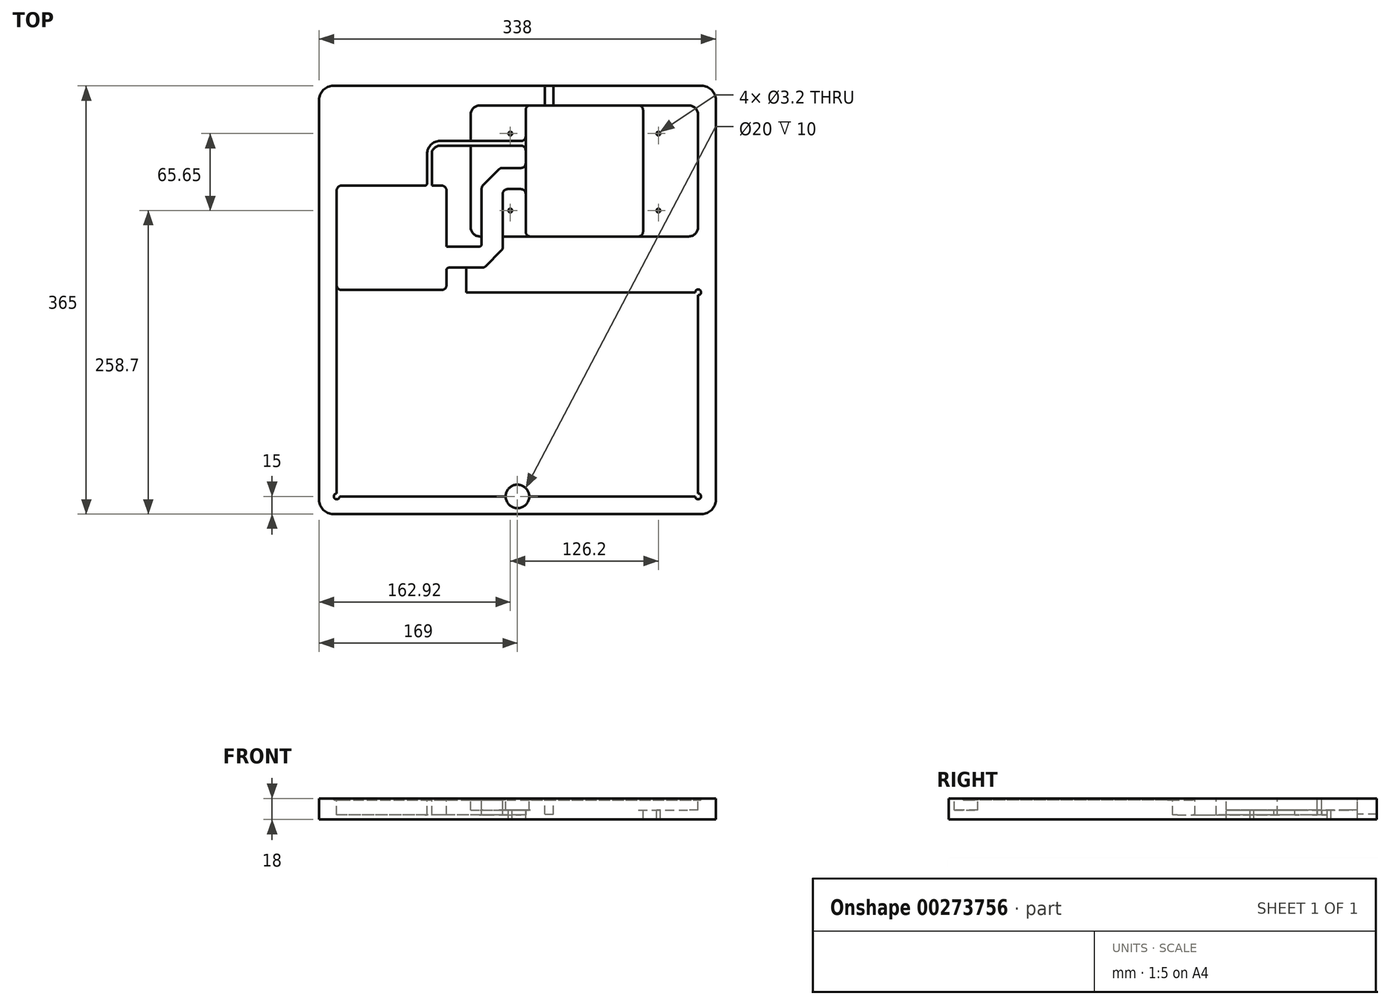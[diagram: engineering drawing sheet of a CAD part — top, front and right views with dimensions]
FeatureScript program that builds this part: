
annotation { "Feature Type Name" : "Feature", "Feature Type Description" : "" }
export const myFeature = defineFeature(function(context is Context, id is Id, definition is map)
    precondition{}
    {
        {
            var Q0;
            Q0=qCreatedBy(makeId("Top.planeOp"),FACE);
            var sketch = newSketch(context, id + "F0", { "sketchPlane" : qUnion([Q0])});
            skLineSegment(sketch, "E0.bottom", {"start": v(-169, -182.5) * mm, "end": v(169, -182.5) * mm});
            skLineSegment(sketch, "E0.top", {"start": v(-169, 182.5) * mm, "end": v(169, 182.5) * mm});
            skLineSegment(sketch, "E0.left", {"start": v(-169, -182.5) * mm, "end": v(-169, 182.5) * mm});
            skLineSegment(sketch, "E0.right", {"start": v(169, -182.5) * mm, "end": v(169, 182.5) * mm});
            skPoint(sketch, "E0.middle", {"position": v(0, 0) * mm});
            skSolve(sketch);
        }
        {
            var Q0;
            Q0=makeQuery(id+"F0.imprint","IMPRINT",FACE,{"disambiguationData":[TD([[makeQuery(id+"F0.imprint","IMPRINT",EDGE,{"derivedFrom":sQuery(id+"F0.wireOp",EDGE,"E0.bottom")}),1.0]])]});
            extrude(context, id + "F1", {"entities" : qUnion([Q0]), "depth" : 18 * mm});
        }
        {
            var Q0;
            Q0=makeQuery(id+"F1.opExtrude","SWEPT_EDGE",EDGE,{"disambiguationData":[OSD([sQuery(id+"F0.wireOp",EDGE,"E0.top"),sQuery(id+"F0.wireOp",EDGE,"E0.left")])]});
            var Q1;
            Q1=makeQuery(id+"F1.opExtrude","SWEPT_EDGE",EDGE,{"disambiguationData":[OSD([sQuery(id+"F0.wireOp",EDGE,"E0.top"),sQuery(id+"F0.wireOp",EDGE,"E0.right")])]});
            var Q2;
            Q2=makeQuery(id+"F1.opExtrude","SWEPT_EDGE",EDGE,{"disambiguationData":[OSD([sQuery(id+"F0.wireOp",EDGE,"E0.bottom"),sQuery(id+"F0.wireOp",EDGE,"E0.left")])]});
            var Q3;
            Q3=makeQuery(id+"F1.opExtrude","SWEPT_EDGE",EDGE,{"disambiguationData":[OSD([sQuery(id+"F0.wireOp",EDGE,"E0.bottom"),sQuery(id+"F0.wireOp",EDGE,"E0.right")])]});
            fillet(context, id + "F2", {"entities" : qUnion([Q0, Q1, Q2, Q3]), "radius" : 12 * mm, "tangentPropagation" : true, "allowEdgeOverflow" : false});
        }
        {
            var Q0;
            Q0=makeQuery(id+"F1.opExtrude","CAP_FACE",FACE,{"disambiguationData":[OSD([sQuery(id+"F0.wireOp",EDGE,"E0.bottom"),sQuery(id+"F0.wireOp",EDGE,"E0.top"),sQuery(id+"F0.wireOp",EDGE,"E0.left"),sQuery(id+"F0.wireOp",EDGE,"E0.right")])],"isStart":false});
            var sketch = newSketch(context, id + "F3", { "sketchPlane" : qUnion([Q0])});
            skLineSegment(sketch, "E1.bottom", {"start": v(-60.5, 8.5) * mm, "end": v(-149.5, 8.5) * mm});
            skLineSegment(sketch, "E1.top", {"start": v(-60.5, 66.5) * mm, "end": v(-149.5, 66.5) * mm});
            skLineSegment(sketch, "E1.left", {"start": v(-60.5, 8.5) * mm, "end": v(-60.5, 66.5) * mm});
            skLineSegment(sketch, "E1.right", {"start": v(-149.5, 8.5) * mm, "end": v(-149.5, 66.5) * mm});
            skPoint(sketch, "E1.middle", {"position": v(-105, 37.5) * mm});
            skLineSegment(sketch, "E2.bottom", {"start": v(-154, 6.5) * mm, "end": v(154, 6.5) * mm});
            skLineSegment(sketch, "E2.top", {"start": v(-154, -167.5) * mm, "end": v(154, -167.5) * mm});
            skLineSegment(sketch, "E2.left", {"start": v(-154, 6.5) * mm, "end": v(-154, -167.5) * mm});
            skLineSegment(sketch, "E2.right", {"start": v(154, 6.5) * mm, "end": v(154, -167.5) * mm});
            skPoint(sketch, "E3", {"position": v(0, -167.5) * mm});
            skLineSegment(sketch, "E4.bottom", {"start": v(-154, 40.5) * mm, "end": v(-43.5, 40.5) * mm});
            skLineSegment(sketch, "E4.top", {"start": v(-154, 0.5) * mm, "end": v(-43.5, 0.5) * mm});
            skLineSegment(sketch, "E4.left", {"start": v(-154, 40.5) * mm, "end": v(-154, 0.5) * mm});
            skLineSegment(sketch, "E4.right", {"start": v(-43.5, 40.5) * mm, "end": v(-43.5, 0.5) * mm});
            skLineSegment(sketch, "E5.bottom", {"start": v(-31.96, 165.38) * mm, "end": v(146, 165.38) * mm, "construction": true});
            skLineSegment(sketch, "E5.top", {"start": v(-31.96, 54.62) * mm, "end": v(146, 54.62) * mm, "construction": true});
            skLineSegment(sketch, "E5.left", {"start": v(-39.46, 157.88) * mm, "end": v(-39.46, 62.12) * mm, "construction": true});
            skLineSegment(sketch, "E5.right", {"start": v(153.5, 157.88) * mm, "end": v(153.5, 62.12) * mm, "construction": true});
            skCircle(sketch, "E6", {"center": v(-154, -6) * mm, "radius": 12.5 * mm, "construction": true});
            skCircle(sketch, "E7", {"center": v(-154, -155) * mm, "radius": 12.5 * mm, "construction": true});
            skCircle(sketch, "E8", {"center": v(154, 8.5) * mm, "radius": 12.5 * mm, "construction": true});
            skCircle(sketch, "E9", {"center": v(154, -155) * mm, "radius": 12.5 * mm, "construction": true});
            skLineSegment(sketch, "E10", {"start": v(-39.46, 165.38) * mm, "end": v(153.5, 54.62) * mm, "construction": true});
            skPoint(sketch, "E11.visualSharp", {"position": v(-39.46, 165.38) * mm});
            skArc(sketch, "E11.filletArc", {"start": v(-31.96, 165.38) * mm, "mid": v(-37.26, 163.18) * mm, "end": v(-39.46, 157.88) * mm, "construction": true});
            skPoint(sketch, "E12.visualSharp", {"position": v(-39.46, 54.62) * mm});
            skArc(sketch, "E12.filletArc", {"start": v(-39.46, 62.12) * mm, "mid": v(-37.26, 56.82) * mm, "end": v(-31.96, 54.62) * mm, "construction": true});
            skPoint(sketch, "E13.visualSharp", {"position": v(153.5, 165.38) * mm});
            skArc(sketch, "E13.filletArc", {"start": v(153.5, 157.88) * mm, "mid": v(151.3, 163.18) * mm, "end": v(146, 165.38) * mm, "construction": true});
            skPoint(sketch, "E14.visualSharp", {"position": v(153.5, 54.62) * mm});
            skArc(sketch, "E14.filletArc", {"start": v(146, 54.62) * mm, "mid": v(151.3, 56.82) * mm, "end": v(153.5, 62.12) * mm, "construction": true});
            skLineSegment(sketch, "E15.0", {"start": v(-31.96, 165.88) * mm, "end": v(146, 165.88) * mm});
            skArc(sketch, "E15.1", {"start": v(154, 157.88) * mm, "mid": v(151.66, 163.54) * mm, "end": v(146, 165.88) * mm});
            skArc(sketch, "E15.2", {"start": v(-31.96, 165.88) * mm, "mid": v(-37.62, 163.54) * mm, "end": v(-39.96, 157.88) * mm});
            skLineSegment(sketch, "E15.3", {"start": v(154, 157.88) * mm, "end": v(154, 62.12) * mm});
            skLineSegment(sketch, "E15.4", {"start": v(-39.96, 157.88) * mm, "end": v(-39.96, 62.12) * mm});
            skArc(sketch, "E15.5", {"start": v(-39.96, 62.12) * mm, "mid": v(-37.62, 56.46) * mm, "end": v(-31.96, 54.12) * mm});
            skLineSegment(sketch, "E15.6", {"start": v(-31.96, 54.12) * mm, "end": v(146, 54.12) * mm});
            skArc(sketch, "E15.7", {"start": v(146, 54.12) * mm, "mid": v(151.66, 56.46) * mm, "end": v(154, 62.12) * mm});
            skLineSegment(sketch, "E16.bottom", {"start": v(107.02, 165.38) * mm, "end": v(7.02, 165.38) * mm});
            skLineSegment(sketch, "E16.top", {"start": v(107.02, 54.62) * mm, "end": v(7.02, 54.62) * mm});
            skLineSegment(sketch, "E16.right", {"start": v(7.02, 165.38) * mm, "end": v(7.02, 54.62) * mm});
            skPoint(sketch, "E16.middle", {"position": v(57.02, 110) * mm});
            skLineSegment(sketch, "E17", {"start": v(-49.2, 36.5) * mm, "end": v(-60.5, 36.5) * mm, "construction": true});
            skLineSegment(sketch, "E18", {"start": v(-60.5, 45.5) * mm, "end": v(-49.2, 45.5) * mm, "construction": true});
            skLineSegment(sketch, "E19", {"start": v(-49.2, 45.5) * mm, "end": v(-49.2, 27.5) * mm, "construction": true});
            skLineSegment(sketch, "E20", {"start": v(-49.2, 27.5) * mm, "end": v(-60.5, 27.5) * mm, "construction": true});
            skCircle(sketch, "E21", {"center": v(-6.08, 141.85) * mm, "radius": 1.6 * mm, "construction": true});
            skCircle(sketch, "E22", {"center": v(-6.08, 76.2) * mm, "radius": 1.6 * mm, "construction": true});
            skLineSegment(sketch, "E23", {"start": v(57.02, 110) * mm, "end": v(57.02, 167.5) * mm, "construction": true});
            skCircle(sketch, "E24.MirrorC", {"center": v(120.12, 141.85) * mm, "radius": 1.6 * mm, "construction": true});
            skCircle(sketch, "E25.MirrorC", {"center": v(120.12, 76.2) * mm, "radius": 1.6 * mm, "construction": true});
            skLineSegment(sketch, "E26", {"start": v(-6.08, 141.85) * mm, "end": v(120.12, 141.85) * mm, "construction": true});
            skPoint(sketch, "E27", {"position": v(57.02, 141.85) * mm});
            skLineSegment(sketch, "E28", {"start": v(-149.5, 37.5) * mm, "end": v(-60.5, 37.5) * mm, "construction": true});
            skCircle(sketch, "E29", {"center": v(154, 6.5) * mm, "radius": 2.5 * mm, "construction": true});
            skLineSegment(sketch, "E30", {"start": v(154, 62.12) * mm, "end": v(154, 6.5) * mm, "construction": true});
            skLineSegment(sketch, "E31", {"start": v(-154, 40.5) * mm, "end": v(-154, 66.5) * mm});
            skLineSegment(sketch, "E32", {"start": v(-154, 66.5) * mm, "end": v(-149.5, 66.5) * mm});
            skLineSegment(sketch, "E33", {"start": v(-149.5, 8.5) * mm, "end": v(-154, 8.5) * mm});
            skLineSegment(sketch, "E34", {"start": v(-60.5, 37.5) * mm, "end": v(-60.5, 40.5) * mm});
            skLineSegment(sketch, "E35", {"start": v(0, -167.5) * mm, "end": v(0, -182.5) * mm});
            skLineSegment(sketch, "E36", {"start": v(57.02, 167.5) * mm, "end": v(57.02, 182.5) * mm, "construction": true});
            skLineSegment(sketch, "E37", {"start": v(7.02, 64.62) * mm, "end": v(107.02, 64.62) * mm});
            skLineSegment(sketch, "E38.trimOffspring", {"start": v(107.02, 165.38) * mm, "end": v(107.02, 54.62) * mm});
            skLineSegment(sketch, "E39", {"start": v(7.02, 165.38) * mm, "end": v(7.02, 165.88) * mm});
            skLineSegment(sketch, "E40", {"start": v(107.02, 165.38) * mm, "end": v(107.02, 165.88) * mm});
            skLineSegment(sketch, "E41", {"start": v(107.02, 54.62) * mm, "end": v(107.02, 54.12) * mm});
            skLineSegment(sketch, "E42", {"start": v(7.02, 54.62) * mm, "end": v(7.02, 54.12) * mm});
            skSolve(sketch);
        }
        {
            var Q0;
            {var subQ0=sQuery(id+"F3.wireOp",EDGE,"E1.left");var subQ1=sQuery(id+"F3.wireOp",EDGE,"E1.bottom");var subQ2=makeQuery(id+"F3.imprint","INTERSECT",VERTEX,{"derivedFrom":[subQ1,subQ0]});Q0=makeQuery(id+"F3.imprint","IMPRINT",FACE,{"disambiguationData":[TD([[makeQuery(id+"F3.imprint","IMPRINT",EDGE,{"disambiguationData":[TD([[subQ2,-1.0]])],"derivedFrom":subQ1}),-1.0]])]});}
            var Q1;
            {var subQ1=sQuery(id+"F3.wireOp",EDGE,"E1.top");Q1=makeQuery(id+"F3.imprint","IMPRINT",FACE,{"disambiguationData":[TD([[makeQuery(id+"F3.imprint","IMPRINT",EDGE,{"derivedFrom":subQ1}),1.0]])]});}
            var Q2;
            {var subQ0=sQuery(id+"F3.wireOp",EDGE,"E1.right");var subQ1=sQuery(id+"F3.wireOp",EDGE,"E1.bottom");var subQ2=makeQuery(id+"F3.imprint","INTERSECT",VERTEX,{"derivedFrom":[subQ1,subQ0]});Q2=makeQuery(id+"F3.imprint","IMPRINT",FACE,{"disambiguationData":[TD([[makeQuery(id+"F3.imprint","IMPRINT",EDGE,{"disambiguationData":[TD([[subQ2,1.0]])],"derivedFrom":subQ1}),-1.0]])]});}
            var Q3;
            {var subQ4=sQuery(id+"F3.wireOp",EDGE,"E31");Q3=makeQuery(id+"F3.imprint","IMPRINT",FACE,{"disambiguationData":[TD([[makeQuery(id+"F3.imprint","IMPRINT",EDGE,{"derivedFrom":subQ4}),-1.0]])]});}
            var Q4;
            {var subQ0=sQuery(id+"F3.wireOp",EDGE,"E33");Q4=makeQuery(id+"F3.imprint","IMPRINT",FACE,{"disambiguationData":[TD([[makeQuery(id+"F3.imprint","IMPRINT",EDGE,{"derivedFrom":subQ0}),-1.0]])]});}
            extrude(context, id + "F4", {"entities" : qUnion([Q0, Q1, Q2, Q3, Q4]), "operationType" : NewBodyOperationType.REMOVE, "oppositeDirection" : true, "depth" : 14 * mm});
        }
        {
            var Q0;
            {var subQ18=sQuery(id+"F3.wireOp",EDGE,"E4.top");Q0=makeQuery(id+"F3.imprint","IMPRINT",FACE,{"disambiguationData":[TD([[makeQuery(id+"F3.imprint","IMPRINT",EDGE,{"derivedFrom":subQ18}),-1.0]])]});}
            var Q1;
            {var subQ1=sQuery(id+"F3.wireOp",EDGE,"BiHuEt5s-7Evh-3HVs-5xS8-5UpfKd4jXBis");var subQ2=sQuery(id+"F3.wireOp",EDGE,"E2.bottom");var subQ4=makeQuery(id+"F3.imprint","INTERSECT",VERTEX,{"derivedFrom":[subQ2,subQ1]});Q1=makeQuery(id+"F3.imprint","IMPRINT",FACE,{"disambiguationData":[TD([[makeQuery(id+"F3.imprint","IMPRINT",EDGE,{"disambiguationData":[TD([[subQ4,1.0]])],"derivedFrom":subQ1}),1.0]])]});}
            var Q2;
            {var subQ0=sQuery(id+"F3.wireOp",EDGE,"E6");var subQ1=sQuery(id+"F3.wireOp",EDGE,"BiHuEt5s-7Evh-3HVs-5xS8-5UpfKd4jXBis");var subQ3=makeQuery(id+"F3.imprint","INTERSECT",VERTEX,{"derivedFrom":[subQ1,subQ0]});Q2=makeQuery(id+"F3.imprint","IMPRINT",FACE,{"disambiguationData":[TD([[makeQuery(id+"F3.imprint","IMPRINT",EDGE,{"disambiguationData":[TD([[subQ3,1.0]])],"derivedFrom":subQ1}),1.0]])]});}
            var Q3;
            {var subQ0=sQuery(id+"F3.wireOp",EDGE,"E6");var subQ2=sQuery(id+"F3.wireOp",EDGE,"E2.left");var subQ4=makeQuery(id+"F3.imprint","INTERSECT",VERTEX,{"derivedFrom":[subQ2,subQ0]});Q3=makeQuery(id+"F3.imprint","IMPRINT",FACE,{"disambiguationData":[TD([[makeQuery(id+"F3.imprint","IMPRINT",EDGE,{"disambiguationData":[TD([[subQ4,-1.0]])],"derivedFrom":subQ0}),1.0]])]});}
            var Q4;
            {var subQ5=sQuery(id+"F3.wireOp",EDGE,"E4.top");Q4=makeQuery(id+"F3.imprint","IMPRINT",FACE,{"disambiguationData":[TD([[makeQuery(id+"F3.imprint","IMPRINT",EDGE,{"derivedFrom":subQ5}),1.0]])]});}
            var Q5;
            {var subQ1=sQuery(id+"F3.wireOp",EDGE,"vfooCfW6-rHmT-6K3o-WgXj-G9icVkGturG6");var subQ2=sQuery(id+"F3.wireOp",EDGE,"E2.bottom");var subQ4=makeQuery(id+"F3.imprint","INTERSECT",VERTEX,{"derivedFrom":[subQ2,subQ1]});Q5=makeQuery(id+"F3.imprint","IMPRINT",FACE,{"disambiguationData":[TD([[makeQuery(id+"F3.imprint","IMPRINT",EDGE,{"disambiguationData":[TD([[subQ4,-1.0]])],"derivedFrom":subQ1}),1.0]])]});}
            var Q6;
            {var subQ0=sQuery(id+"F3.wireOp",EDGE,"E8");var subQ1=sQuery(id+"F3.wireOp",EDGE,"vfooCfW6-rHmT-6K3o-WgXj-G9icVkGturG6");var subQ3=makeQuery(id+"F3.imprint","INTERSECT",VERTEX,{"derivedFrom":[subQ1,subQ0]});Q6=makeQuery(id+"F3.imprint","IMPRINT",FACE,{"disambiguationData":[TD([[makeQuery(id+"F3.imprint","IMPRINT",EDGE,{"disambiguationData":[TD([[subQ3,-1.0]])],"derivedFrom":subQ1}),1.0]])]});}
            var Q7;
            {var subQ0=sQuery(id+"F3.wireOp",EDGE,"E8");var subQ2=sQuery(id+"F3.wireOp",EDGE,"E2.right");var subQ4=makeQuery(id+"F3.imprint","INTERSECT",VERTEX,{"derivedFrom":[subQ2,subQ0]});Q7=makeQuery(id+"F3.imprint","IMPRINT",FACE,{"disambiguationData":[TD([[makeQuery(id+"F3.imprint","IMPRINT",EDGE,{"disambiguationData":[TD([[subQ4,1.0]])],"derivedFrom":subQ0}),1.0]])]});}
            var Q8;
            {var subQ0=sQuery(id+"F3.wireOp",EDGE,"E9");var subQ2=sQuery(id+"F3.wireOp",EDGE,"E2.right");var subQ4=makeQuery(id+"F3.imprint","INTERSECT",VERTEX,{"derivedFrom":[subQ2,subQ0]});Q8=makeQuery(id+"F3.imprint","IMPRINT",FACE,{"disambiguationData":[TD([[makeQuery(id+"F3.imprint","IMPRINT",EDGE,{"disambiguationData":[TD([[subQ4,-1.0]])],"derivedFrom":subQ0}),1.0]])]});}
            var Q9;
            {var subQ0=sQuery(id+"F3.wireOp",EDGE,"E9");var subQ1=sQuery(id+"F3.wireOp",EDGE,"zM4nkVd2-yPlo-7xgH-uxup-0wEgS1WaxvJd");var subQ3=makeQuery(id+"F3.imprint","INTERSECT",VERTEX,{"derivedFrom":[subQ1,subQ0]});Q9=makeQuery(id+"F3.imprint","IMPRINT",FACE,{"disambiguationData":[TD([[makeQuery(id+"F3.imprint","IMPRINT",EDGE,{"disambiguationData":[TD([[subQ3,1.0]])],"derivedFrom":subQ1}),1.0]])]});}
            var Q10;
            {var subQ1=sQuery(id+"F3.wireOp",EDGE,"zM4nkVd2-yPlo-7xgH-uxup-0wEgS1WaxvJd");var subQ2=sQuery(id+"F3.wireOp",EDGE,"E2.top");var subQ4=makeQuery(id+"F3.imprint","INTERSECT",VERTEX,{"derivedFrom":[subQ2,subQ1]});Q10=makeQuery(id+"F3.imprint","IMPRINT",FACE,{"disambiguationData":[TD([[makeQuery(id+"F3.imprint","IMPRINT",EDGE,{"disambiguationData":[TD([[subQ4,1.0]])],"derivedFrom":subQ1}),1.0]])]});}
            var Q11;
            {var subQ1=sQuery(id+"F3.wireOp",EDGE,"nX78Pxld-BHQV-mbCp-fKfu-vvGhQssENttC");var subQ2=sQuery(id+"F3.wireOp",EDGE,"E2.top");var subQ4=makeQuery(id+"F3.imprint","INTERSECT",VERTEX,{"derivedFrom":[subQ2,subQ1]});Q11=makeQuery(id+"F3.imprint","IMPRINT",FACE,{"disambiguationData":[TD([[makeQuery(id+"F3.imprint","IMPRINT",EDGE,{"disambiguationData":[TD([[subQ4,-1.0]])],"derivedFrom":subQ1}),1.0]])]});}
            var Q12;
            {var subQ0=sQuery(id+"F3.wireOp",EDGE,"E7");var subQ1=sQuery(id+"F3.wireOp",EDGE,"nX78Pxld-BHQV-mbCp-fKfu-vvGhQssENttC");var subQ3=makeQuery(id+"F3.imprint","INTERSECT",VERTEX,{"derivedFrom":[subQ1,subQ0]});Q12=makeQuery(id+"F3.imprint","IMPRINT",FACE,{"disambiguationData":[TD([[makeQuery(id+"F3.imprint","IMPRINT",EDGE,{"disambiguationData":[TD([[subQ3,-1.0]])],"derivedFrom":subQ1}),1.0]])]});}
            var Q13;
            {var subQ0=sQuery(id+"F3.wireOp",EDGE,"E7");var subQ2=sQuery(id+"F3.wireOp",EDGE,"E2.left");var subQ4=makeQuery(id+"F3.imprint","INTERSECT",VERTEX,{"derivedFrom":[subQ2,subQ0]});Q13=makeQuery(id+"F3.imprint","IMPRINT",FACE,{"disambiguationData":[TD([[makeQuery(id+"F3.imprint","IMPRINT",EDGE,{"disambiguationData":[TD([[subQ4,1.0]])],"derivedFrom":subQ0}),1.0]])]});}
            extrude(context, id + "F5", {"entities" : qUnion([Q0, Q1, Q2, Q3, Q4, Q5, Q6, Q7, Q8, Q9, Q10, Q11, Q12, Q13]), "operationType" : NewBodyOperationType.REMOVE, "oppositeDirection" : true, "depth" : 1.5 * mm});
        }
        {
            var Q0;
            {var subQ2=sQuery(id+"F3.wireOp",EDGE,"E15.2");Q0=makeQuery(id+"F3.imprint","IMPRINT",FACE,{"disambiguationData":[TD([[makeQuery(id+"F3.imprint","IMPRINT",EDGE,{"derivedFrom":subQ2}),1.0]])]});}
            var Q1;
            Q1=makeQuery(id+"F3.imprint","IMPRINT",FACE,{"disambiguationData":[TD([[makeQuery(id+"F3.imprint","IMPRINT",EDGE,{"derivedFrom":sQuery(id+"F3.wireOp",EDGE,"E16.bottom")}),1.0]])]});
            var Q2;
            {var subQ3=sQuery(id+"F3.wireOp",EDGE,"E15.1");Q2=makeQuery(id+"F3.imprint","IMPRINT",FACE,{"disambiguationData":[TD([[makeQuery(id+"F3.imprint","IMPRINT",EDGE,{"derivedFrom":subQ3}),1.0]])]});}
            var Q3;
            {var subQ0=sQuery(id+"F3.wireOp",EDGE,"E16.top");Q3=makeQuery(id+"F3.imprint","IMPRINT",FACE,{"disambiguationData":[TD([[makeQuery(id+"F3.imprint","IMPRINT",EDGE,{"derivedFrom":subQ0}),-1.0]])]});}
            var Q4;
            Q4=makeQuery(id+"F3.imprint","IMPRINT",FACE,{"disambiguationData":[TD([[makeQuery(id+"F3.imprint","IMPRINT",EDGE,{"derivedFrom":sQuery(id+"F3.wireOp",EDGE,"E16.bottom")}),-1.0]])]});
            var Q5;
            Q5=makeQuery(id+"F3.imprint","IMPRINT",FACE,{"disambiguationData":[TD([[makeQuery(id+"F3.imprint","IMPRINT",EDGE,{"derivedFrom":sQuery(id+"F3.wireOp",EDGE,"E16.top")}),1.0]])]});
            extrude(context, id + "F6", {"entities" : qUnion([Q0, Q1, Q2, Q3, Q4, Q5]), "operationType" : NewBodyOperationType.REMOVE, "oppositeDirection" : true, "depth" : 10 * mm});
        }
        {
            var Q0;
            Q0=makeQuery(id+"F3.imprint","IMPRINT",FACE,{"disambiguationData":[TD([[makeQuery(id+"F3.imprint","IMPRINT",EDGE,{"derivedFrom":sQuery(id+"F3.wireOp",EDGE,"E16.bottom")}),-1.0]])]});
            var Q1;
            {var subQ0=sQuery(id+"F3.wireOp",EDGE,"E16.bottom");Q1=makeQuery(id+"F3.imprint","IMPRINT",FACE,{"disambiguationData":[TD([[makeQuery(id+"F3.imprint","IMPRINT",EDGE,{"derivedFrom":subQ0}),1.0]])]});}
            var Q2;
            {var subQ0=sQuery(id+"F3.wireOp",EDGE,"E16.top");Q2=makeQuery(id+"F3.imprint","IMPRINT",FACE,{"disambiguationData":[TD([[makeQuery(id+"F3.imprint","IMPRINT",EDGE,{"derivedFrom":subQ0}),-1.0]])]});}
            var Q3;
            Q3=makeQuery(id+"F3.imprint","IMPRINT",FACE,{"disambiguationData":[TD([[makeQuery(id+"F3.imprint","IMPRINT",EDGE,{"derivedFrom":sQuery(id+"F3.wireOp",EDGE,"E16.top")}),1.0]])]});
            extrude(context, id + "F7", {"entities" : qUnion([Q0, Q1, Q2, Q3]), "operationType" : NewBodyOperationType.REMOVE, "endBound" : BoundingType.THROUGH_ALL, "oppositeDirection" : true, "depth" : 11 * mm});
        }
        {
            var Q0;
            {var subQ3=sQuery(id+"F3.wireOp",EDGE,"E1.left");var subQ5=sQuery(id+"F3.wireOp",EDGE,"E1.bottom");var subQ6=makeQuery(id+"F3.imprint","INTERSECT",VERTEX,{"derivedFrom":[subQ5,subQ3]});Q0=makeQuery(id+"F3.imprint","IMPRINT",FACE,{"disambiguationData":[TD([[makeQuery(id+"F3.imprint","IMPRINT",EDGE,{"disambiguationData":[TD([[subQ6,-1.0]])],"derivedFrom":subQ5}),1.0]])]});}
            var Q1;
            {var subQ5=sQuery(id+"F3.wireOp",EDGE,"E4.top");Q1=makeQuery(id+"F3.imprint","IMPRINT",FACE,{"disambiguationData":[TD([[makeQuery(id+"F3.imprint","IMPRINT",EDGE,{"derivedFrom":subQ5}),1.0]])]});}
            var Q2;
            {var subQ0=sQuery(id+"F3.wireOp",EDGE,"E1.left");var subQ1=sQuery(id+"F3.wireOp",EDGE,"E1.bottom");var subQ2=makeQuery(id+"F3.imprint","INTERSECT",VERTEX,{"derivedFrom":[subQ1,subQ0]});Q2=makeQuery(id+"F3.imprint","IMPRINT",FACE,{"disambiguationData":[TD([[makeQuery(id+"F3.imprint","IMPRINT",EDGE,{"disambiguationData":[TD([[subQ2,-1.0]])],"derivedFrom":subQ1}),-1.0]])]});}
            var Q3;
            Q3=makeQuery(id+"F5.boolean.opBoolean","COPY",FACE,{"derivedFrom":makeQuery(id+"F5.opExtrude","CAP_FACE",FACE,{"disambiguationData":[OSD([sQuery(id+"F3.wireOp",EDGE,"E2.bottom"),sQuery(id+"F3.wireOp",EDGE,"E2.top"),sQuery(id+"F3.wireOp",EDGE,"E2.left"),sQuery(id+"F3.wireOp",EDGE,"E2.right")])],"isStart":false})});
            extrude(context, id + "F8", {"entities" : qUnion([Q0, Q1, Q2]), "operationType" : NewBodyOperationType.REMOVE, "endBound" : BoundingType.UP_TO_SURFACE, "oppositeDirection" : true, "endBoundEntityFace" : qUnion([Q3]), "depth" : 25 * mm});
        }
        {
            var Q0;
            {var subQ20=sQuery(id+"F3.wireOp",EDGE,"E1.top");Q0=makeQuery(id+"F3.imprint","IMPRINT",FACE,{"disambiguationData":[TD([[makeQuery(id+"F3.imprint","IMPRINT",EDGE,{"derivedFrom":subQ20}),-1.0]])]});}
            var sketch = newSketch(context, id + "F9", { "sketchPlane" : qUnion([Q0])});
            skLineSegment(sketch, "E43.bottom", {"start": v(-154, 97.5) * mm, "end": v(-60.5, 97.5) * mm});
            skLineSegment(sketch, "E43.top", {"start": v(-154, 8.5) * mm, "end": v(-60.5, 8.5) * mm});
            skLineSegment(sketch, "E43.left", {"start": v(-154, 97.5) * mm, "end": v(-154, 8.5) * mm});
            skLineSegment(sketch, "E43.right", {"start": v(-60.5, 97.5) * mm, "end": v(-60.5, 8.5) * mm});
            skPoint(sketch, "E44.visualSharp", {"position": v(-60.5, 97.5) * mm});
            skPoint(sketch, "E45.visualSharp", {"position": v(-154, 97.5) * mm});
            skSolve(sketch);
        }
        {
            var Q0;
            {var subQ2=sQuery(id+"F9.wireOp",EDGE,"E43.bottom");Q0=makeQuery(id+"F9.imprint","IMPRINT",FACE,{"disambiguationData":[TD([[makeQuery(id+"F9.imprint","IMPRINT",EDGE,{"derivedFrom":subQ2}),-1.0]])]});}
            var Q1;
            {var subQ5=sQuery(id+"F9.wireOp",EDGE,"E43.top");Q1=makeQuery(id+"F9.imprint","IMPRINT",FACE,{"disambiguationData":[TD([[makeQuery(id+"F9.imprint","IMPRINT",EDGE,{"derivedFrom":subQ5}),1.0]])]});}
            var Q2;
            Q2=makeQuery(id+"F4.boolean.opBoolean","COPY",FACE,{"derivedFrom":makeQuery(id+"F4.opExtrude","CAP_FACE",FACE,{"disambiguationData":[OSD([sQuery(id+"F3.wireOp",EDGE,"E1.bottom"),sQuery(id+"F3.wireOp",EDGE,"E1.top"),sQuery(id+"F3.wireOp",EDGE,"E1.left"),sQuery(id+"F3.wireOp",EDGE,"E1.right")])],"isStart":false})});
            extrude(context, id + "F10", {"entities" : qUnion([Q0, Q1]), "operationType" : NewBodyOperationType.REMOVE, "endBound" : BoundingType.UP_TO_SURFACE, "oppositeDirection" : true, "endBoundEntityFace" : qUnion([Q2]), "depth" : 5 * mm});
        }
        {
            var Q0;
            {var subQ20=sQuery(id+"F3.wireOp",EDGE,"E1.top");Q0=makeQuery(id+"F3.imprint","IMPRINT",FACE,{"disambiguationData":[TD([[makeQuery(id+"F3.imprint","IMPRINT",EDGE,{"derivedFrom":subQ20}),-1.0]])]});}
            var sketch = newSketch(context, id + "F11", { "sketchPlane" : qUnion([Q0])});
            skLineSegment(sketch, "E46.bottom", {"start": v(25.37, 182.5) * mm, "end": v(30.37, 182.5) * mm});
            skLineSegment(sketch, "E46.top", {"start": v(25.37, 165.38) * mm, "end": v(30.37, 165.38) * mm, "construction": true});
            skLineSegment(sketch, "E46.left", {"start": v(25.37, 182.5) * mm, "end": v(25.37, 165.38) * mm});
            skLineSegment(sketch, "E46.right", {"start": v(30.37, 182.5) * mm, "end": v(30.37, 165.38) * mm});
            skLineSegment(sketch, "E47", {"start": v(27.87, 182.5) * mm, "end": v(27.87, 165.38) * mm, "construction": true});
            skLineSegment(sketch, "E48", {"start": v(25.37, 165.38) * mm, "end": v(25.37, 165.38) * mm});
            skLineSegment(sketch, "E49", {"start": v(25.37, 165.38) * mm, "end": v(30.37, 165.38) * mm});
            skLineSegment(sketch, "E50", {"start": v(30.37, 165.38) * mm, "end": v(30.37, 165.38) * mm});
            skSolve(sketch);
        }
        {
            var Q0;
            {var subQ20=sQuery(id+"F3.wireOp",EDGE,"E1.top");Q0=makeQuery(id+"F3.imprint","IMPRINT",FACE,{"disambiguationData":[TD([[makeQuery(id+"F3.imprint","IMPRINT",EDGE,{"derivedFrom":subQ20}),-1.0]])]});}
            var sketch = newSketch(context, id + "F12", { "sketchPlane" : qUnion([Q0])});
            skCircle(sketch, "E51.0", {"center": v(-6.08, 141.85) * mm, "radius": 1.6 * mm});
            skCircle(sketch, "E51.1", {"center": v(-6.08, 76.2) * mm, "radius": 1.6 * mm});
            skCircle(sketch, "E51.2", {"center": v(120.12, 76.2) * mm, "radius": 1.6 * mm});
            skCircle(sketch, "E51.3", {"center": v(120.12, 141.85) * mm, "radius": 1.6 * mm});
            skSolve(sketch);
        }
        {
            var Q0;
            Q0 = qSketchRegion(id + "F12", true);
            var Q1;
            Q1=sQuery(id+"F12.wireOp",EDGE,"E51.0");
            var Q2;
            Q2=sQuery(id+"F12.wireOp",EDGE,"E51.1");
            var Q3;
            Q3=sQuery(id+"F12.wireOp",EDGE,"E51.2");
            var Q4;
            Q4=sQuery(id+"F12.wireOp",EDGE,"E51.3");
            extrude(context, id + "F13", {"entities" : qUnion([Q0]), "operationType" : NewBodyOperationType.REMOVE, "surfaceEntities" : qUnion([Q1, Q2, Q3, Q4]), "endBound" : BoundingType.THROUGH_ALL, "oppositeDirection" : true, "depth" : 25 * mm});
        }
        {
            var Q0;
            Q0=makeQuery(id+"F1.opExtrude","CAP_FACE",FACE,{"disambiguationData":[OSD([sQuery(id+"F0.wireOp",EDGE,"E0.bottom"),sQuery(id+"F0.wireOp",EDGE,"E0.top"),sQuery(id+"F0.wireOp",EDGE,"E0.left"),sQuery(id+"F0.wireOp",EDGE,"E0.right")])],"isStart":false});
            var sketch = newSketch(context, id + "F14", { "sketchPlane" : qUnion([Q0])});
            skLineSegment(sketch, "E52", {"start": v(-77, 97.5) * mm, "end": v(-77, 182.5) * mm});
            skLineSegment(sketch, "E53.3", {"start": v(-73, 97.5) * mm, "end": v(-73, 124.5) * mm});
            skLineSegment(sketch, "E54", {"start": v(-77, 182.5) * mm, "end": v(-73, 182.5) * mm});
            skLineSegment(sketch, "E55", {"start": v(-77, 97.5) * mm, "end": v(-73, 97.5) * mm});
            skPoint(sketch, "E56", {"position": v(-75, 97.5) * mm});
            skLineSegment(sketch, "E57", {"start": v(-66, 131.5) * mm, "end": v(18.53, 131.5) * mm});
            skLineSegment(sketch, "E58", {"start": v(-77, 135.5) * mm, "end": v(18.53, 135.5) * mm});
            skLineSegment(sketch, "E59", {"start": v(18.53, 135.5) * mm, "end": v(18.53, 131.5) * mm});
            skArc(sketch, "E60.filletArc", {"start": v(-66, 131.5) * mm, "mid": v(-70.95, 129.45) * mm, "end": v(-73, 124.5) * mm});
            skArc(sketch, "E61", {"start": v(-66, 135.5) * mm, "mid": v(-73.78, 132.28) * mm, "end": v(-77, 124.5) * mm});
            skSolve(sketch);
        }
        {
            var Q0;
            Q0=makeQuery(id+"F14.imprint","IMPRINT",FACE,{"disambiguationData":[TD([[makeQuery(id+"F14.imprint","IMPRINT",EDGE,{"derivedFrom":sQuery(id+"F14.wireOp",EDGE,"E53.3")}),1.0]])]});
            var Q1;
            {var subQ0=sQuery(id+"F14.wireOp",EDGE,"E59");Q1=makeQuery(id+"F14.imprint","IMPRINT",FACE,{"disambiguationData":[TD([[makeQuery(id+"F14.imprint","IMPRINT",EDGE,{"derivedFrom":subQ0}),-1.0]])]});}
            var Q2;
            Q2=makeQuery(id+"F4.boolean.opBoolean","COPY",FACE,{"derivedFrom":makeQuery(id+"F4.opExtrude","CAP_FACE",FACE,{"disambiguationData":[OSD([sQuery(id+"F3.wireOp",EDGE,"E1.bottom"),sQuery(id+"F3.wireOp",EDGE,"E1.top"),sQuery(id+"F3.wireOp",EDGE,"E1.left"),sQuery(id+"F3.wireOp",EDGE,"E1.right")])],"isStart":false})});
            extrude(context, id + "F15", {"entities" : qUnion([Q0, Q1]), "operationType" : NewBodyOperationType.REMOVE, "endBound" : BoundingType.UP_TO_SURFACE, "oppositeDirection" : true, "endBoundEntityFace" : qUnion([Q2]), "depth" : 25 * mm});
        }
        {
            var Q0;
            {var subQ25=sQuery(id+"F3.wireOp",EDGE,"E1.top");Q0=makeQuery(id+"F3.imprint","IMPRINT",FACE,{"disambiguationData":[TD([[makeQuery(id+"F3.imprint","IMPRINT",EDGE,{"derivedFrom":subQ25}),-1.0]])]});}
            var sketch = newSketch(context, id + "F16", { "sketchPlane" : qUnion([Q0])});
            skLineSegment(sketch, "E62", {"start": v(-60.5, 45.5) * mm, "end": v(-30.5, 45.5) * mm});
            skLineSegment(sketch, "E63", {"start": v(-60.5, 45.5) * mm, "end": v(-60.5, 27.5) * mm});
            skLineSegment(sketch, "E64", {"start": v(-60.5, 27.5) * mm, "end": v(-30.5, 27.5) * mm});
            skLineSegment(sketch, "E65", {"start": v(-30.5, 27.5) * mm, "end": v(-12.5, 45.5) * mm, "construction": true});
            skLineSegment(sketch, "E66", {"start": v(-30.5, 27.5) * mm, "end": v(-30.5, 45.5) * mm, "construction": true});
            skLineSegment(sketch, "E67", {"start": v(-30.5, 45.5) * mm, "end": v(-12.5, 45.5) * mm});
            skLineSegment(sketch, "E68", {"start": v(-12.5, 45.5) * mm, "end": v(-12.5, 94.5) * mm});
            skLineSegment(sketch, "E69", {"start": v(-12.5, 94.5) * mm, "end": v(36.58, 94.5) * mm});
            skLineSegment(sketch, "E70", {"start": v(36.58, 94.5) * mm, "end": v(36.58, 112.5) * mm});
            skLineSegment(sketch, "E71", {"start": v(36.58, 112.5) * mm, "end": v(-12.5, 112.5) * mm});
            skLineSegment(sketch, "E72", {"start": v(-12.5, 112.5) * mm, "end": v(-30.5, 94.5) * mm, "construction": true});
            skLineSegment(sketch, "E73", {"start": v(-30.5, 94.5) * mm, "end": v(-30.5, 45.5) * mm});
            skPoint(sketch, "E74", {"position": v(36.58, 103.5) * mm});
            skLineSegment(sketch, "E75", {"start": v(-12.5, 45.5) * mm, "end": v(-12.5, 43.38) * mm});
            skLineSegment(sketch, "E76", {"start": v(-12.5, 43.38) * mm, "end": v(-28.38, 27.5) * mm});
            skLineSegment(sketch, "E77", {"start": v(-28.38, 27.5) * mm, "end": v(-30.5, 27.5) * mm});
            skLineSegment(sketch, "E78", {"start": v(-30.5, 94.5) * mm, "end": v(-30.5, 96.62) * mm});
            skLineSegment(sketch, "E79", {"start": v(-30.5, 96.62) * mm, "end": v(-14.62, 112.5) * mm});
            skLineSegment(sketch, "E80", {"start": v(-14.62, 112.5) * mm, "end": v(-12.5, 112.5) * mm});
            skSolve(sketch);
        }
        {
            var Q0;
            {var subQ0=sQuery(id+"F16.wireOp",EDGE,"E69");Q0=makeQuery(id+"F16.imprint","IMPRINT",FACE,{"disambiguationData":[TD([[makeQuery(id+"F16.imprint","IMPRINT",EDGE,{"derivedFrom":subQ0}),1.0]])]});}
            var Q1;
            {var subQ0=sQuery(id+"F16.wireOp",EDGE,"E67");Q1=makeQuery(id+"F16.imprint","IMPRINT",FACE,{"disambiguationData":[TD([[makeQuery(id+"F16.imprint","IMPRINT",EDGE,{"derivedFrom":subQ0}),1.0]])]});}
            var Q2;
            {var subQ1=sQuery(id+"F3.wireOp",EDGE,"E4.right");var subQ2=sQuery(id+"F3.wireOp",EDGE,"E4.bottom");var subQ3=makeQuery(id+"F3.imprint","INTERSECT",VERTEX,{"derivedFrom":[subQ2,subQ1]});var subQ4=makeQuery(id+"F3.imprint","IMPRINT",EDGE,{"disambiguationData":[TD([[subQ3,1.0]])],"derivedFrom":subQ2});Q2=makeQuery(id+"F16.imprint","IMPRINT",FACE,{"disambiguationData":[TD([[makeQuery(id+"F16.imprint","IMPRINT",EDGE,{"derivedFrom":subQ4}),-1.0]])]});}
            var Q3;
            {var subQ11=sQuery(id+"F16.wireOp",EDGE,"E62");Q3=makeQuery(id+"F16.imprint","IMPRINT",FACE,{"disambiguationData":[TD([[makeQuery(id+"F16.imprint","IMPRINT",EDGE,{"derivedFrom":subQ11}),-1.0]])]});}
            var Q4;
            {var subQ0=sQuery(id+"F3.wireOp",EDGE,"E34");var subQ1=sQuery(id+"F3.wireOp",EDGE,"E33");var subQ2=sQuery(id+"F3.wireOp",EDGE,"E32");var subQ3=sQuery(id+"F3.wireOp",EDGE,"E31");var subQ4=sQuery(id+"F3.wireOp",EDGE,"E4.left");var subQ5=sQuery(id+"F3.wireOp",EDGE,"E1.left");var subQ6=sQuery(id+"F3.wireOp",EDGE,"E1.top");var subQ7=sQuery(id+"F3.wireOp",EDGE,"E1.bottom");Q4=makeQuery(id+"F15.boolean.opBoolean","MERGE",FACE,{"derivedFrom":[makeQuery(id+"F10.boolean.opBoolean","MERGE",FACE,{"derivedFrom":[makeQuery(id+"F4.boolean.opBoolean","COPY",FACE,{"derivedFrom":makeQuery(id+"F4.opExtrude","CAP_FACE",FACE,{"disambiguationData":[OSD([subQ7,subQ6,subQ5,subQ4,subQ3,subQ2,subQ1,subQ0])],"isStart":false})}),makeQuery(id+"F10.opExtrude","CAP_FACE",FACE,{"disambiguationData":[OSD([subQ7,subQ6,subQ5,subQ4,subQ3,subQ2,subQ1,subQ0])],"isStart":false})]}),makeQuery(id+"F15.opExtrude","CAP_FACE",FACE,{"disambiguationData":[OSD([subQ7,subQ6,subQ5,subQ4,subQ3,subQ2,subQ1,subQ0])],"isStart":false})]});}
            extrude(context, id + "F17", {"entities" : qUnion([Q0, Q1, Q2, Q3]), "operationType" : NewBodyOperationType.REMOVE, "endBound" : BoundingType.UP_TO_SURFACE, "oppositeDirection" : true, "endBoundEntityFace" : qUnion([Q4]), "depth" : 25 * mm});
        }
        {
            var Q0;
            Q0=makeQuery(id+"F16.imprint","IMPRINT",FACE,{"disambiguationData":[TD([[makeQuery(id+"F16.imprint","IMPRINT",EDGE,{"derivedFrom":sQuery(id+"F16.wireOp",EDGE,"E67")}),1.0]])]});
            var Q1;
            {var subQ7=sQuery(id+"F16.wireOp",EDGE,"E67");Q1=makeQuery(id+"F16.imprint","IMPRINT",FACE,{"disambiguationData":[TD([[makeQuery(id+"F16.imprint","IMPRINT",EDGE,{"derivedFrom":subQ7}),-1.0]])]});}
            var Q2;
            {var subQ1=sQuery(id+"F3.wireOp",EDGE,"E4.right");var subQ2=sQuery(id+"F3.wireOp",EDGE,"E4.bottom");var subQ3=makeQuery(id+"F3.imprint","INTERSECT",VERTEX,{"derivedFrom":[subQ2,subQ1]});var subQ4=makeQuery(id+"F3.imprint","IMPRINT",EDGE,{"disambiguationData":[TD([[subQ3,1.0]])],"derivedFrom":subQ2});Q2=makeQuery(id+"F16.imprint","IMPRINT",FACE,{"disambiguationData":[TD([[makeQuery(id+"F16.imprint","IMPRINT",EDGE,{"derivedFrom":subQ4}),-1.0]])]});}
            var Q3;
            {var subQ0=sQuery(id+"F16.wireOp",EDGE,"E69");Q3=makeQuery(id+"F16.imprint","IMPRINT",FACE,{"disambiguationData":[TD([[makeQuery(id+"F16.imprint","IMPRINT",EDGE,{"derivedFrom":subQ0}),1.0]])]});}
            var Q4;
            {var subQ0=sQuery(id+"F3.wireOp",EDGE,"E34");var subQ1=sQuery(id+"F3.wireOp",EDGE,"E33");var subQ2=sQuery(id+"F3.wireOp",EDGE,"E32");var subQ3=sQuery(id+"F3.wireOp",EDGE,"E31");var subQ4=sQuery(id+"F3.wireOp",EDGE,"E4.left");var subQ5=sQuery(id+"F3.wireOp",EDGE,"E1.left");var subQ6=sQuery(id+"F3.wireOp",EDGE,"E1.top");var subQ7=sQuery(id+"F3.wireOp",EDGE,"E1.bottom");Q4=makeQuery(id+"F17.boolean.opBoolean","MERGE",FACE,{"derivedFrom":[makeQuery(id+"F15.boolean.opBoolean","MERGE",FACE,{"derivedFrom":[makeQuery(id+"F10.boolean.opBoolean","MERGE",FACE,{"derivedFrom":[makeQuery(id+"F4.boolean.opBoolean","COPY",FACE,{"derivedFrom":makeQuery(id+"F4.opExtrude","CAP_FACE",FACE,{"disambiguationData":[OSD([subQ7,subQ6,subQ5,subQ4,subQ3,subQ2,subQ1,subQ0])],"isStart":false})}),makeQuery(id+"F10.opExtrude","CAP_FACE",FACE,{"disambiguationData":[OSD([subQ7,subQ6,subQ5,subQ4,subQ3,subQ2,subQ1,subQ0])],"isStart":false})]}),makeQuery(id+"F15.opExtrude","CAP_FACE",FACE,{"disambiguationData":[OSD([subQ7,subQ6,subQ5,subQ4,subQ3,subQ2,subQ1,subQ0])],"isStart":false})]}),makeQuery(id+"F17.opExtrude","CAP_FACE",FACE,{"disambiguationData":[OSD([subQ7,subQ6,subQ5,subQ4,subQ3,subQ2,subQ1,subQ0])],"isStart":false})]});}
            extrude(context, id + "F18", {"entities" : qUnion([Q0, Q1, Q2, Q3]), "operationType" : NewBodyOperationType.REMOVE, "endBound" : BoundingType.UP_TO_SURFACE, "oppositeDirection" : true, "endBoundEntityFace" : qUnion([Q4]), "depth" : 12 * mm});
        }
        {
            var Q0;
            {var subQ2=sQuery(id+"F0.wireOp",EDGE,"E0.top");var subQ3=sQuery(id+"F0.wireOp",EDGE,"E0.right");var subQ4=sQuery(id+"F0.wireOp",EDGE,"E0.left");var subQ6=sQuery(id+"F0.wireOp",EDGE,"E0.bottom");Q0=makeQuery(id+"F17.boolean.opBoolean","SPLIT",FACE,{"disambiguationData":[TD([makeQuery(id+"F1.opExtrude","SWEPT_FACE",FACE,{"disambiguationData":[OSD([subQ6])]})])],"derivedFrom":makeQuery(id+"F1.opExtrude","CAP_FACE",FACE,{"disambiguationData":[OSD([subQ6,subQ2,subQ4,subQ3])],"isStart":false})});}
            var sketch = newSketch(context, id + "F19", { "sketchPlane" : qUnion([Q0])});
            skCircle(sketch, "E81", {"center": v(154, 6.5) * mm, "radius": 2.5 * mm});
            skCircle(sketch, "E82", {"center": v(-154, -167.5) * mm, "radius": 2.5 * mm});
            skCircle(sketch, "E83", {"center": v(154, -167.5) * mm, "radius": 2.5 * mm});
            skSolve(sketch);
        }
        {
            var Q0;
            Q0=makeQuery(id+"F17.boolean.opBoolean","COPY",EDGE,{"derivedFrom":makeQuery(id+"F17.opExtrude","SWEPT_EDGE",EDGE,{"disambiguationData":[OSD([sQuery(id+"F16.wireOp",EDGE,"E62"),sQuery(id+"F16.wireOp",EDGE,"E67"),sQuery(id+"F16.wireOp",EDGE,"E73")])]})});
            var Q1;
            Q1=makeQuery(id+"F17.boolean.opBoolean","COPY",EDGE,{"derivedFrom":makeQuery(id+"F17.opExtrude","SWEPT_EDGE",EDGE,{"disambiguationData":[OSD([sQuery(id+"F3.wireOp",EDGE,"E1.left"),sQuery(id+"F16.wireOp",EDGE,"E62"),sQuery(id+"F16.wireOp",EDGE,"E63")])]})});
            var Q2;
            Q2=makeQuery(id+"F17.boolean.opBoolean","COPY",EDGE,{"derivedFrom":makeQuery(id+"F17.opExtrude","SWEPT_EDGE",EDGE,{"disambiguationData":[OSD([sQuery(id+"F16.wireOp",EDGE,"E63"),sQuery(id+"F16.wireOp",EDGE,"E64")])]})});
            var Q3;
            Q3=makeQuery(id+"F15.boolean.opBoolean","COPY",EDGE,{"derivedFrom":makeQuery(id+"F15.opExtrude","SWEPT_EDGE",EDGE,{"disambiguationData":[OSD([sQuery(id+"F9.wireOp",EDGE,"E43.bottom"),sQuery(id+"F14.wireOp",EDGE,"E52"),sQuery(id+"F14.wireOp",EDGE,"E55")])]})});
            var Q4;
            Q4=makeQuery(id+"F15.boolean.opBoolean","COPY",EDGE,{"derivedFrom":makeQuery(id+"F15.opExtrude","SWEPT_EDGE",EDGE,{"disambiguationData":[OSD([sQuery(id+"F9.wireOp",EDGE,"E43.bottom"),sQuery(id+"F14.wireOp",EDGE,"E53.3"),sQuery(id+"F14.wireOp",EDGE,"E55")])]})});
            var Q5;
            Q5=makeQuery(id+"F15.boolean.opBoolean","COPY",EDGE,{"derivedFrom":makeQuery(id+"F15.opExtrude","SWEPT_EDGE",EDGE,{"disambiguationData":[OSD([sQuery(id+"F0.wireOp",EDGE,"E0.top"),sQuery(id+"F14.wireOp",EDGE,"E52"),sQuery(id+"F14.wireOp",EDGE,"E54")])]})});
            var Q6;
            Q6=makeQuery(id+"F15.boolean.opBoolean","COPY",EDGE,{"derivedFrom":makeQuery(id+"F15.opExtrude","SWEPT_EDGE",EDGE,{"disambiguationData":[OSD([sQuery(id+"F0.wireOp",EDGE,"E0.top"),sQuery(id+"F14.wireOp",EDGE,"E53.3"),sQuery(id+"F14.wireOp",EDGE,"E54")])]})});
            fillet(context, id + "F20", {"entities" : qUnion([Q0, Q1, Q2, Q3, Q4, Q5, Q6]), "radius" : 2 * mm, "tangentPropagation" : true, "allowEdgeOverflow" : false});
        }
        {
            var Q0;
            {var subQ0=sQuery(id+"F19.wireOp",EDGE,"E81");var subQ1=sQuery(id+"F3.wireOp",EDGE,"E2.right");var subQ2=makeQuery(id+"F5.boolean.opBoolean","COPY",EDGE,{"derivedFrom":makeQuery(id+"F5.opExtrude","CAP_EDGE",EDGE,{"disambiguationData":[OSD([subQ1])],"isStart":true})});var subQ3=makeQuery(id+"F19.imprint","INTERSECT",VERTEX,{"derivedFrom":[subQ2,subQ0]});Q0=makeQuery(id+"F19.imprint","IMPRINT",FACE,{"disambiguationData":[TD([[makeQuery(id+"F19.imprint","IMPRINT",EDGE,{"disambiguationData":[TD([[subQ3,-1.0]])],"derivedFrom":subQ0}),1.0]])]});}
            var Q1;
            {var subQ0=sQuery(id+"F19.wireOp",EDGE,"E83");var subQ1=makeQuery(id+"F5.boolean.opBoolean","COPY",EDGE,{"derivedFrom":makeQuery(id+"F5.opExtrude","CAP_EDGE",EDGE,{"disambiguationData":[OSD([sQuery(id+"F3.wireOp",EDGE,"E2.top")])],"isStart":true})});var subQ2=makeQuery(id+"F19.imprint","INTERSECT",VERTEX,{"derivedFrom":[subQ1,subQ0]});Q1=makeQuery(id+"F19.imprint","IMPRINT",FACE,{"disambiguationData":[TD([[makeQuery(id+"F19.imprint","IMPRINT",EDGE,{"disambiguationData":[TD([[subQ2,-1.0]])],"derivedFrom":subQ0}),1.0]])]});}
            var Q2;
            {var subQ0=sQuery(id+"F19.wireOp",EDGE,"E82");var subQ1=makeQuery(id+"F5.boolean.opBoolean","COPY",EDGE,{"derivedFrom":makeQuery(id+"F5.opExtrude","CAP_EDGE",EDGE,{"disambiguationData":[OSD([sQuery(id+"F3.wireOp",EDGE,"E2.top")])],"isStart":true})});var subQ2=makeQuery(id+"F19.imprint","INTERSECT",VERTEX,{"derivedFrom":[subQ1,subQ0]});Q2=makeQuery(id+"F19.imprint","IMPRINT",FACE,{"disambiguationData":[TD([[makeQuery(id+"F19.imprint","IMPRINT",EDGE,{"disambiguationData":[TD([[subQ2,1.0]])],"derivedFrom":subQ0}),1.0]])]});}
            var Q3;
            {var subQ0=sQuery(id+"F3.wireOp",EDGE,"E2.right");var subQ1=sQuery(id+"F3.wireOp",EDGE,"E2.left");var subQ2=sQuery(id+"F3.wireOp",EDGE,"E2.top");var subQ3=sQuery(id+"F3.wireOp",EDGE,"E2.bottom");Q3=makeQuery(id+"F8.boolean.opBoolean","MERGE",FACE,{"derivedFrom":[makeQuery(id+"F5.boolean.opBoolean","COPY",FACE,{"derivedFrom":makeQuery(id+"F5.opExtrude","CAP_FACE",FACE,{"disambiguationData":[OSD([subQ3,subQ2,subQ1,subQ0])],"isStart":false})}),makeQuery(id+"F8.opExtrude","CAP_FACE",FACE,{"disambiguationData":[OSD([subQ3,subQ2,subQ1,subQ0])],"isStart":false})]});}
            extrude(context, id + "F21", {"entities" : qUnion([Q0, Q1, Q2]), "operationType" : NewBodyOperationType.REMOVE, "endBound" : BoundingType.UP_TO_SURFACE, "oppositeDirection" : true, "endBoundEntityFace" : qUnion([Q3]), "depth" : 25 * mm});
        }
        {
            var Q0;
            {var subQ2=sQuery(id+"F0.wireOp",EDGE,"E0.top");var subQ3=sQuery(id+"F0.wireOp",EDGE,"E0.right");var subQ4=sQuery(id+"F0.wireOp",EDGE,"E0.left");var subQ6=sQuery(id+"F0.wireOp",EDGE,"E0.bottom");Q0=makeQuery(id+"F17.boolean.opBoolean","SPLIT",FACE,{"disambiguationData":[TD([makeQuery(id+"F1.opExtrude","SWEPT_FACE",FACE,{"disambiguationData":[OSD([subQ6])]})])],"derivedFrom":makeQuery(id+"F1.opExtrude","CAP_FACE",FACE,{"disambiguationData":[OSD([subQ6,subQ2,subQ4,subQ3])],"isStart":false})});}
            var sketch = newSketch(context, id + "F22", { "sketchPlane" : qUnion([Q0])});
            skCircle(sketch, "E84", {"center": v(0, -167.5) * mm, "radius": 10 * mm});
            skSolve(sketch);
        }
        {
            var Q0;
            {var subQ0=sQuery(id+"F22.wireOp",EDGE,"E84");var subQ1=makeQuery(id+"F5.boolean.opBoolean","COPY",EDGE,{"derivedFrom":makeQuery(id+"F5.opExtrude","CAP_EDGE",EDGE,{"disambiguationData":[OSD([sQuery(id+"F3.wireOp",EDGE,"E2.top")])],"isStart":true})});var subQ2=makeQuery(id+"F22.imprint","INTERSECT",VERTEX,{"disambiguationData":[OD(0.0)],"derivedFrom":[subQ1,subQ0]});Q0=makeQuery(id+"F22.imprint","IMPRINT",FACE,{"disambiguationData":[TD([[makeQuery(id+"F22.imprint","IMPRINT",EDGE,{"disambiguationData":[TD([[subQ2,1.0]])],"derivedFrom":subQ0}),1.0]])]});}
            var Q1;
            {var subQ0=sQuery(id+"F22.wireOp",EDGE,"E84");var subQ1=makeQuery(id+"F5.boolean.opBoolean","COPY",EDGE,{"derivedFrom":makeQuery(id+"F5.opExtrude","CAP_EDGE",EDGE,{"disambiguationData":[OSD([sQuery(id+"F3.wireOp",EDGE,"E2.top")])],"isStart":true})});var subQ2=makeQuery(id+"F22.imprint","INTERSECT",VERTEX,{"disambiguationData":[OD(0.0)],"derivedFrom":[subQ1,subQ0]});Q1=makeQuery(id+"F22.imprint","IMPRINT",FACE,{"disambiguationData":[TD([[makeQuery(id+"F22.imprint","IMPRINT",EDGE,{"disambiguationData":[TD([[subQ2,-1.0]])],"derivedFrom":subQ0}),1.0]])]});}
            extrude(context, id + "F23", {"entities" : qUnion([Q0, Q1]), "operationType" : NewBodyOperationType.REMOVE, "oppositeDirection" : true, "depth" : 10 * mm});
        }
        {
            var Q0;
            Q0=makeQuery(id+"F1.opExtrude","CAP_FACE",FACE,{"disambiguationData":[OSD([sQuery(id+"F0.wireOp",EDGE,"E0.bottom"),sQuery(id+"F0.wireOp",EDGE,"E0.top"),sQuery(id+"F0.wireOp",EDGE,"E0.left"),sQuery(id+"F0.wireOp",EDGE,"E0.right")])],"isStart":false});
            var sketch = newSketch(context, id + "F24", { "sketchPlane" : qUnion([Q0])});
            skSolve(sketch);
        }
        {
            var Q0;
            {var subQ11=sQuery(id+"F0.wireOp",EDGE,"E0.bottom");Q0=makeQuery(id+"F24.imprint","IMPRINT",FACE,{"disambiguationData":[TD([[makeQuery(id+"F24.imprint","IMPRINT",EDGE,{"derivedFrom":makeQuery(id+"F1.opExtrude","CAP_EDGE",EDGE,{"disambiguationData":[OSD([subQ11])],"isStart":false})}),1.0]])]});}
            var sketch = newSketch(context, id + "F25", { "sketchPlane" : qUnion([Q0])});
            skLineSegment(sketch, "E85.bottom", {"start": v(7.02, 135.5) * mm, "end": v(-54.98, 135.5) * mm});
            skLineSegment(sketch, "E85.top", {"start": v(7.02, 131.5) * mm, "end": v(-54.98, 131.5) * mm});
            skLineSegment(sketch, "E85.left", {"start": v(7.02, 135.5) * mm, "end": v(7.02, 131.5) * mm});
            skLineSegment(sketch, "E85.right", {"start": v(-54.98, 135.5) * mm, "end": v(-54.98, 131.5) * mm});
            skSolve(sketch);
        }
        {
            var Q0;
            {var subQ1=sQuery(id+"F0.wireOp",EDGE,"E0.bottom");var subQ2=sQuery(id+"F0.wireOp",EDGE,"E0.right");var subQ4=sQuery(id+"F0.wireOp",EDGE,"E0.left");var subQ5=sQuery(id+"F0.wireOp",EDGE,"E0.top");Q0=makeQuery(id+"F17.boolean.opBoolean","SPLIT",FACE,{"disambiguationData":[TD([makeQuery(id+"F1.opExtrude","SWEPT_FACE",FACE,{"disambiguationData":[OSD([subQ1])]})])],"derivedFrom":makeQuery(id+"F1.opExtrude","CAP_FACE",FACE,{"disambiguationData":[OSD([subQ1,subQ5,subQ4,subQ2])],"isStart":false})});}
            var sketch = newSketch(context, id + "F26", { "sketchPlane" : qUnion([Q0])});
            skLineSegment(sketch, "E86.bottom", {"start": v(23.52, 182.5) * mm, "end": v(30.52, 182.5) * mm});
            skLineSegment(sketch, "E86.top", {"start": v(23.52, 165.88) * mm, "end": v(30.52, 165.88) * mm});
            skLineSegment(sketch, "E86.left", {"start": v(23.52, 182.5) * mm, "end": v(23.52, 165.88) * mm});
            skLineSegment(sketch, "E86.right", {"start": v(30.52, 182.5) * mm, "end": v(30.52, 165.88) * mm});
            skLineSegment(sketch, "E87", {"start": v(27.02, 182.5) * mm, "end": v(27.02, 165.88) * mm, "construction": true});
            skPoint(sketch, "E88", {"position": v(57.02, 165.88) * mm});
            skSolve(sketch);
        }
        {
            var Q0;
            Q0 = qSketchRegion(id + "F26", true);
            extrude(context, id + "F27", {"entities" : qUnion([Q0]), "operationType" : NewBodyOperationType.REMOVE, "oppositeDirection" : true, "depth" : 13.5 * mm});
        }
        {
            var Q0;
            Q0=makeQuery(id+"F10.boolean.opBoolean","COPY",EDGE,{"derivedFrom":makeQuery(id+"F10.opExtrude","SWEPT_EDGE",EDGE,{"disambiguationData":[OSD([sQuery(id+"F9.wireOp",EDGE,"E43.bottom"),sQuery(id+"F9.wireOp",EDGE,"E43.left")])]})});
            var Q1;
            Q1=makeQuery(id+"F10.boolean.opBoolean","COPY",EDGE,{"derivedFrom":makeQuery(id+"F10.opExtrude","SWEPT_EDGE",EDGE,{"disambiguationData":[OSD([sQuery(id+"F9.wireOp",EDGE,"E43.bottom"),sQuery(id+"F9.wireOp",EDGE,"E43.right")])]})});
            var Q2;
            Q2=makeQuery(id+"F4.boolean.opBoolean","COPY",EDGE,{"derivedFrom":makeQuery(id+"F4.opExtrude","SWEPT_EDGE",EDGE,{"disambiguationData":[OSD([sQuery(id+"F3.wireOp",EDGE,"E1.bottom"),sQuery(id+"F3.wireOp",EDGE,"E1.left")])]})});
            var Q3;
            Q3=makeQuery(id+"F10.boolean.opBoolean","COPY",EDGE,{"derivedFrom":makeQuery(id+"F10.opExtrude","SWEPT_EDGE",EDGE,{"disambiguationData":[OSD([sQuery(id+"F9.wireOp",EDGE,"E43.top"),sQuery(id+"F9.wireOp",EDGE,"E43.left")])]})});
            var Q4;
            Q4=makeQuery(id+"F4.boolean.opBoolean","COPY",EDGE,{"derivedFrom":makeQuery(id+"F4.opExtrude","SWEPT_EDGE",EDGE,{"disambiguationData":[OSD([sQuery(id+"F3.wireOp",EDGE,"E4.left"),sQuery(id+"F3.wireOp",EDGE,"E33")])]})});
            var Q5;
            Q5=makeQuery(id+"F17.boolean.opBoolean","COPY",EDGE,{"derivedFrom":makeQuery(id+"F17.opExtrude","SWEPT_EDGE",EDGE,{"disambiguationData":[OSD([sQuery(id+"F16.wireOp",EDGE,"E65"),sQuery(id+"F16.wireOp",EDGE,"E67"),sQuery(id+"F16.wireOp",EDGE,"E68")])]})});
            var Q6;
            Q6=makeQuery(id+"F17.boolean.opBoolean","COPY",EDGE,{"derivedFrom":makeQuery(id+"F17.opExtrude","SWEPT_EDGE",EDGE,{"disambiguationData":[OSD([sQuery(id+"F16.wireOp",EDGE,"E64"),sQuery(id+"F16.wireOp",EDGE,"E65")])]})});
            var Q7;
            Q7=makeQuery(id+"F17.boolean.opBoolean","COPY",EDGE,{"derivedFrom":makeQuery(id+"F17.opExtrude","SWEPT_EDGE",EDGE,{"disambiguationData":[OSD([sQuery(id+"F16.wireOp",EDGE,"E75"),sQuery(id+"F16.wireOp",EDGE,"E76")])]})});
            var Q8;
            Q8=makeQuery(id+"F17.boolean.opBoolean","COPY",EDGE,{"derivedFrom":makeQuery(id+"F17.opExtrude","SWEPT_EDGE",EDGE,{"disambiguationData":[OSD([sQuery(id+"F16.wireOp",EDGE,"E76"),sQuery(id+"F16.wireOp",EDGE,"E77")])]})});
            var Q9;
            Q9=makeQuery(id+"F7.boolean.opBoolean","COPY",EDGE,{"derivedFrom":makeQuery(id+"F7.opExtrude","SWEPT_EDGE",EDGE,{"disambiguationData":[OSD([sQuery(id+"F3.wireOp",EDGE,"E15.0"),sQuery(id+"F3.wireOp",EDGE,"E16.bottom"),sQuery(id+"F3.wireOp",EDGE,"E16.right")])]})});
            var Q10;
            Q10=makeQuery(id+"F7.boolean.opBoolean","COPY",EDGE,{"derivedFrom":makeQuery(id+"F7.opExtrude","SWEPT_EDGE",EDGE,{"disambiguationData":[OSD([sQuery(id+"F3.wireOp",EDGE,"E15.0"),sQuery(id+"F3.wireOp",EDGE,"E16.bottom"),sQuery(id+"F3.wireOp",EDGE,"E16.left")])]})});
            var Q11;
            Q11=makeQuery(id+"F7.boolean.opBoolean","COPY",EDGE,{"derivedFrom":makeQuery(id+"F7.opExtrude","SWEPT_EDGE",EDGE,{"disambiguationData":[OSD([sQuery(id+"F3.wireOp",EDGE,"E15.6"),sQuery(id+"F3.wireOp",EDGE,"E16.top"),sQuery(id+"F3.wireOp",EDGE,"E16.left")])]})});
            var Q12;
            Q12=makeQuery(id+"F7.boolean.opBoolean","COPY",EDGE,{"derivedFrom":makeQuery(id+"F7.opExtrude","SWEPT_EDGE",EDGE,{"disambiguationData":[OSD([sQuery(id+"F3.wireOp",EDGE,"E15.6"),sQuery(id+"F3.wireOp",EDGE,"E16.top"),sQuery(id+"F3.wireOp",EDGE,"E16.right")])]})});
            var Q13;
            Q13=makeQuery(id+"F17.boolean.opBoolean","COPY",EDGE,{"derivedFrom":makeQuery(id+"F17.opExtrude","SWEPT_EDGE",EDGE,{"disambiguationData":[OSD([sQuery(id+"F16.wireOp",EDGE,"E79"),sQuery(id+"F16.wireOp",EDGE,"E80")])]})});
            var Q14;
            Q14=makeQuery(id+"F17.boolean.opBoolean","COPY",EDGE,{"derivedFrom":makeQuery(id+"F17.opExtrude","SWEPT_EDGE",EDGE,{"disambiguationData":[OSD([sQuery(id+"F16.wireOp",EDGE,"E78"),sQuery(id+"F16.wireOp",EDGE,"E79")])]})});
            var Q15;
            Q15=makeQuery(id+"Ff5NL2PMwhvVNQZ_1.boolean.opBoolean","MERGE",EDGE,{"derivedFrom":[makeQuery(id+"F15.boolean.opBoolean","INTERSECT",EDGE,{"derivedFrom":[makeQuery(id+"F7.boolean.opBoolean","COPY",FACE,{"derivedFrom":makeQuery(id+"F7.opExtrude","SWEPT_FACE",FACE,{"disambiguationData":[OSD([sQuery(id+"F3.wireOp",EDGE,"E16.right")])]})}),makeQuery(id+"F15.opExtrude","SWEPT_FACE",FACE,{"disambiguationData":[OSD([sQuery(id+"F14.wireOp",EDGE,"E57")])]})]}),makeQuery(id+"Ff5NL2PMwhvVNQZ_1.opExtrude","SWEPT_EDGE",EDGE,{"disambiguationData":[OSD([sQuery(id+"F25.wireOp",EDGE,"E85.top"),sQuery(id+"F25.wireOp",EDGE,"E85.left")])]})]});
            var Q16;
            Q16=makeQuery(id+"Ff5NL2PMwhvVNQZ_1.boolean.opBoolean","MERGE",EDGE,{"derivedFrom":[makeQuery(id+"F15.boolean.opBoolean","INTERSECT",EDGE,{"derivedFrom":[makeQuery(id+"F7.boolean.opBoolean","COPY",FACE,{"derivedFrom":makeQuery(id+"F7.opExtrude","SWEPT_FACE",FACE,{"disambiguationData":[OSD([sQuery(id+"F3.wireOp",EDGE,"E16.right")])]})}),makeQuery(id+"F15.opExtrude","SWEPT_FACE",FACE,{"disambiguationData":[OSD([sQuery(id+"F14.wireOp",EDGE,"E58")])]})]}),makeQuery(id+"Ff5NL2PMwhvVNQZ_1.opExtrude","SWEPT_EDGE",EDGE,{"disambiguationData":[OSD([sQuery(id+"F25.wireOp",EDGE,"E85.bottom"),sQuery(id+"F25.wireOp",EDGE,"E85.left")])]})]});
            var Q17;
            Q17=makeQuery(id+"F17.boolean.opBoolean","INTERSECT",EDGE,{"derivedFrom":[makeQuery(id+"F7.boolean.opBoolean","COPY",FACE,{"derivedFrom":makeQuery(id+"F7.opExtrude","SWEPT_FACE",FACE,{"disambiguationData":[OSD([sQuery(id+"F3.wireOp",EDGE,"E16.right")])]})}),makeQuery(id+"F17.opExtrude","SWEPT_FACE",FACE,{"disambiguationData":[OSD([sQuery(id+"F16.wireOp",EDGE,"E71"),sQuery(id+"F16.wireOp",EDGE,"E80")])]})]});
            var Q18;
            Q18=makeQuery(id+"F17.boolean.opBoolean","INTERSECT",EDGE,{"derivedFrom":[makeQuery(id+"F7.boolean.opBoolean","COPY",FACE,{"derivedFrom":makeQuery(id+"F7.opExtrude","SWEPT_FACE",FACE,{"disambiguationData":[OSD([sQuery(id+"F3.wireOp",EDGE,"E16.right")])]})}),makeQuery(id+"F17.opExtrude","SWEPT_FACE",FACE,{"disambiguationData":[OSD([sQuery(id+"F16.wireOp",EDGE,"E69")])]})]});
            fillet(context, id + "F28", {"entities" : qUnion([Q0, Q1, Q2, Q3, Q4, Q5, Q6, Q7, Q8, Q9, Q10, Q11, Q12, Q13, Q14, Q15, Q16, Q17, Q18]), "radius" : 4 * mm, "tangentPropagation" : true, "allowEdgeOverflow" : false});
        }
        {
            var Q0;
            Q0=makeQuery(id+"F23.boolean.opBoolean","INTERSECT",EDGE,{"disambiguationData":[OD(0.0)],"derivedFrom":[makeQuery(id+"F5.boolean.opBoolean","COPY",FACE,{"derivedFrom":makeQuery(id+"F5.opExtrude","SWEPT_FACE",FACE,{"disambiguationData":[OSD([sQuery(id+"F3.wireOp",EDGE,"E2.top")])]})}),makeQuery(id+"F23.opExtrude","SWEPT_FACE",FACE,{"disambiguationData":[OSD([sQuery(id+"F22.wireOp",EDGE,"E84")])]})]});
            var Q1;
            Q1=makeQuery(id+"F23.boolean.opBoolean","INTERSECT",EDGE,{"disambiguationData":[OD(1.0)],"derivedFrom":[makeQuery(id+"F5.boolean.opBoolean","COPY",FACE,{"derivedFrom":makeQuery(id+"F5.opExtrude","SWEPT_FACE",FACE,{"disambiguationData":[OSD([sQuery(id+"F3.wireOp",EDGE,"E2.top")])]})}),makeQuery(id+"F23.opExtrude","SWEPT_FACE",FACE,{"disambiguationData":[OSD([sQuery(id+"F22.wireOp",EDGE,"E84")])]})]});
            var Q2;
            Q2=makeQuery(id+"F21.boolean.opBoolean","COPY",EDGE,{"derivedFrom":makeQuery(id+"F21.opExtrude","SWEPT_EDGE",EDGE,{"disambiguationData":[OSD([sQuery(id+"F3.wireOp",EDGE,"E2.left"),sQuery(id+"F3.wireOp",EDGE,"E4.left"),sQuery(id+"F3.wireOp",EDGE,"E31"),sQuery(id+"F9.wireOp",EDGE,"E43.left"),sQuery(id+"F19.wireOp",EDGE,"E82")])]})});
            var Q3;
            Q3=makeQuery(id+"F21.boolean.opBoolean","COPY",EDGE,{"derivedFrom":makeQuery(id+"F21.opExtrude","SWEPT_EDGE",EDGE,{"disambiguationData":[OSD([sQuery(id+"F3.wireOp",EDGE,"E2.top"),sQuery(id+"F19.wireOp",EDGE,"E82")])]})});
            var Q4;
            Q4=makeQuery(id+"F21.boolean.opBoolean","COPY",EDGE,{"derivedFrom":makeQuery(id+"F21.opExtrude","SWEPT_EDGE",EDGE,{"disambiguationData":[OSD([sQuery(id+"F3.wireOp",EDGE,"E2.right"),sQuery(id+"F19.wireOp",EDGE,"E81")])]})});
            var Q5;
            Q5=makeQuery(id+"F21.boolean.opBoolean","COPY",EDGE,{"derivedFrom":makeQuery(id+"F21.opExtrude","SWEPT_EDGE",EDGE,{"disambiguationData":[OSD([sQuery(id+"F3.wireOp",EDGE,"E2.bottom"),sQuery(id+"F19.wireOp",EDGE,"E81")])]})});
            var Q6;
            Q6=makeQuery(id+"F21.boolean.opBoolean","COPY",EDGE,{"derivedFrom":makeQuery(id+"F21.opExtrude","SWEPT_EDGE",EDGE,{"disambiguationData":[OSD([sQuery(id+"F3.wireOp",EDGE,"E2.right"),sQuery(id+"F19.wireOp",EDGE,"E83")])]})});
            var Q7;
            Q7=makeQuery(id+"F21.boolean.opBoolean","COPY",EDGE,{"derivedFrom":makeQuery(id+"F21.opExtrude","SWEPT_EDGE",EDGE,{"disambiguationData":[OSD([sQuery(id+"F3.wireOp",EDGE,"E2.top"),sQuery(id+"F19.wireOp",EDGE,"E83")])]})});
            fillet(context, id + "F29", {"entities" : qUnion([Q0, Q1, Q2, Q3, Q4, Q5, Q6, Q7]), "radius" : 2 * mm, "tangentPropagation" : true, "allowEdgeOverflow" : false});
        }
    });
